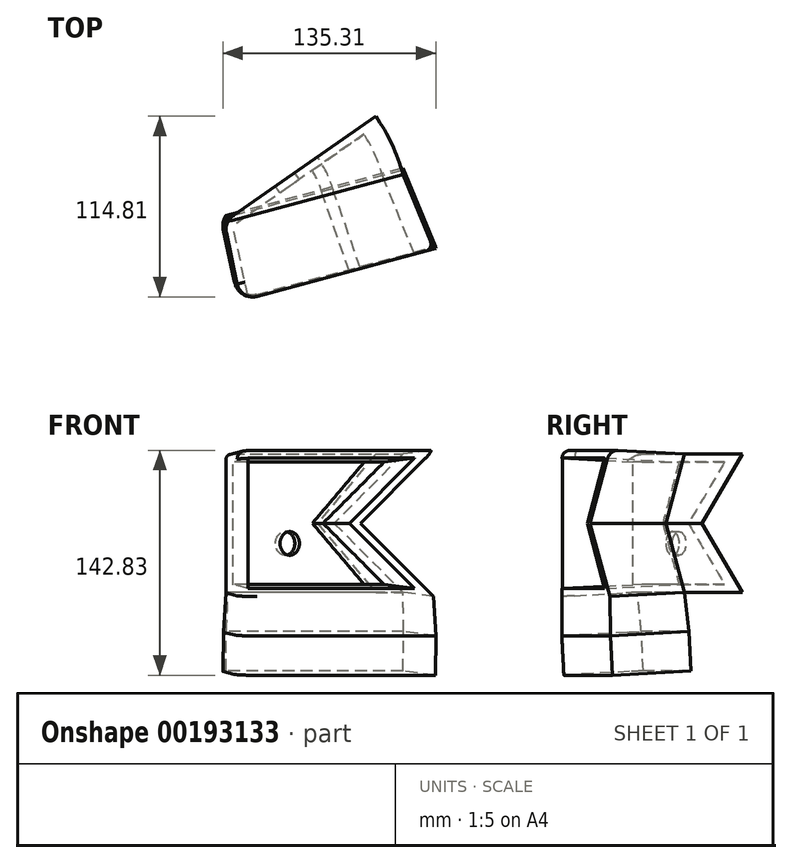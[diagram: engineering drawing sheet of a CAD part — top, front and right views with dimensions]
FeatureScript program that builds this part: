
annotation { "Feature Type Name" : "Feature", "Feature Type Description" : "" }
export const myFeature = defineFeature(function(context is Context, id is Id, definition is map)
    precondition{}
    {
        {
            var Q0;
            Q0=qCreatedBy(makeId("Front.planeOp"),FACE);
            var sketch = newSketch(context, id + "F0", { "sketchPlane" : qUnion([Q0])});
            skLineSegment(sketch, "E0", {"start": v(0, 0) * mm, "end": v(-58.78, 0) * mm});
            skLineSegment(sketch, "E1", {"start": v(-58.78, 0) * mm, "end": v(-58.78, 43.89) * mm});
            skLineSegment(sketch, "E2", {"start": v(-58.78, 43.89) * mm, "end": v(0, 43.89) * mm});
            skLineSegment(sketch, "E3", {"start": v(0, 43.89) * mm, "end": v(-22.61, 21.94) * mm});
            skPoint(sketch, "E3.endSnap0", {"position": v(-58.78, 21.94) * mm});
            skLineSegment(sketch, "E4", {"start": v(-22.61, 21.94) * mm, "end": v(0, 0) * mm});
            skSolve(sketch);
        }
        {
            var Q0;
            Q0=makeQuery(id+"F0.imprint","IMPRINT",FACE,{"disambiguationData":[TD([[makeQuery(id+"F0.imprint","IMPRINT",EDGE,{"derivedFrom":sQuery(id+"F0.wireOp",EDGE,"E0")}),-1.0]])]});
            var Q1;
            Q1=sQuery(id+"F0.wireOp",EDGE,"E1");
            revolve(context, id + "F1", {"entities" : qUnion([Q0]), "axis" : qUnion([Q1]), "revolveType" : RevolveType.TWO_DIRECTIONS, "angle" : 35 * degree, "angleBack" : 15 * degree});
        }
        {
            var Q0;
            Q0=makeQuery(id+"F1.opRevolve","CAP_FACE",FACE,{"disambiguationData":[OSD([sQuery(id+"F0.wireOp",EDGE,"E0"),sQuery(id+"F0.wireOp",EDGE,"E1"),sQuery(id+"F0.wireOp",EDGE,"E2"),sQuery(id+"F0.wireOp",EDGE,"E3"),sQuery(id+"F0.wireOp",EDGE,"E4")])],"isStart":true});
            extrude(context, id + "F2", {"entities" : qUnion([Q0]), "operationType" : NewBodyOperationType.ADD, "depth" : 25.4 * mm, "hasDraft" : true, "draftAngle" : 3 * degree});
        }
        {
            var Q0;
            Q0=makeQuery(id+"F2.opExtrude","CAP_FACE",FACE,{"disambiguationData":[OSD([sQuery(id+"F0.wireOp",EDGE,"E0"),sQuery(id+"F0.wireOp",EDGE,"E1"),sQuery(id+"F0.wireOp",EDGE,"E2"),sQuery(id+"F0.wireOp",EDGE,"E3"),sQuery(id+"F0.wireOp",EDGE,"E4")])],"isStart":false});
            shell(context, id + "F3", {"entities" : qUnion([Q0]), "thickness" : 2.54 * mm});
        }
        {
            var Q0;
            Q0=makeQuery(id+"F2.opExtrude","CAP_EDGE",EDGE,{"disambiguationData":[OSD([sQuery(id+"F0.wireOp",EDGE,"E1")])],"isStart":false});
            fillet(context, id + "F4", {"entities" : qUnion([Q0]), "radius" : 5.08 * mm, "tangentPropagation" : true, "allowEdgeOverflow" : false});
        }
        {
            var Q0;
            {var subQ0=sQuery(id+"F0.wireOp",EDGE,"E1");Q0=makeQuery(id+"F2.boolean.opBoolean","MERGE",EDGE,{"derivedFrom":[makeQuery(id+"F1.opRevolve","CAP_EDGE",EDGE,{"disambiguationData":[OSD([subQ0])],"isStart":true}),makeQuery(id+"F2.opExtrude","CAP_EDGE",EDGE,{"disambiguationData":[OSD([subQ0])],"isStart":true})]});}
            fillet(context, id + "F5", {"entities" : qUnion([Q0]), "radius" : 5.08 * mm, "tangentPropagation" : true, "allowEdgeOverflow" : false});
        }
        {
            var Q0;
            Q0=makeQuery(id+"F2.opExtrude","SWEPT_EDGE",EDGE,{"disambiguationData":[OSD([sQuery(id+"F0.wireOp",EDGE,"E1"),sQuery(id+"F0.wireOp",EDGE,"E2")])]});
            fillet(context, id + "F6", {"entities" : qUnion([Q0]), "radius" : 2.54 * mm, "tangentPropagation" : true, "allowEdgeOverflow" : false});
        }
        {
            var Q0;
            Q0=makeQuery(id+"F1.opRevolve","SWEPT_BODY",BODY,{"disambiguationData":[OSD([sQuery(id+"F0.wireOp",EDGE,"E0"),sQuery(id+"F0.wireOp",EDGE,"E1"),sQuery(id+"F0.wireOp",EDGE,"E2"),sQuery(id+"F0.wireOp",EDGE,"E3"),sQuery(id+"F0.wireOp",EDGE,"E4")])]});
            var Q1;
            {var subQ0=sQuery(id+"F0.wireOp",EDGE,"E2");Q1=makeQuery(id+"F6.opFillet","BLEND_VERTEX",VERTEX,{"blendedFrom":[makeQuery(id+"F2.opExtrude","CAP_EDGE",EDGE,{"disambiguationData":[OSD([subQ0])],"isStart":false}),makeQuery(id+"F2.opExtrude","SWEPT_FACE",FACE,{"disambiguationData":[OSD([sQuery(id+"F0.wireOp",EDGE,"E3")])]}),makeQuery(id+"F2.opExtrude","SWEPT_FACE",FACE,{"disambiguationData":[OSD([subQ0])]})],"blendedInto":[makeQuery(id+"F2.opExtrude","SWEPT_FACE",FACE,{"disambiguationData":[OSD([sQuery(id+"F0.wireOp",EDGE,"E3")])]}),makeQuery(id+"F2.opExtrude","SWEPT_FACE",FACE,{"disambiguationData":[OSD([subQ0])]})]});}
            transform(context, id + "F7", {"entities" : qUnion([Q0]), "transformType" : TransformType.SCALE_UNIFORMLY, "scale" : 2, "scalePoint" : qUnion([Q1]), "makeCopy" : false});
        }
        {
            var Q0;
            Q0=makeQuery(id+"F1.opRevolve","CAP_FACE",FACE,{"disambiguationData":[OSD([sQuery(id+"F0.wireOp",EDGE,"E0"),sQuery(id+"F0.wireOp",EDGE,"E1"),sQuery(id+"F0.wireOp",EDGE,"E2"),sQuery(id+"F0.wireOp",EDGE,"E3"),sQuery(id+"F0.wireOp",EDGE,"E4")])],"isStart":false});
            var sketch = newSketch(context, id + "F8", { "sketchPlane" : qUnion([Q0])});
            skCircle(sketch, "E5", {"center": v(51.07, -14) * mm, "radius": 8.25 * mm});
            skSolve(sketch);
        }
        {
            var Q0;
            Q0=sQuery(id+"F8.wireOp",VERTEX,"E5.center");
            var Q1;
            Q1=makeQuery(id+"F1.opRevolve","SWEPT_BODY",BODY,{"disambiguationData":[OSD([sQuery(id+"F0.wireOp",EDGE,"E0"),sQuery(id+"F0.wireOp",EDGE,"E1"),sQuery(id+"F0.wireOp",EDGE,"E2"),sQuery(id+"F0.wireOp",EDGE,"E3"),sQuery(id+"F0.wireOp",EDGE,"E4")])]});
            hole(context, id + "F9", {"style" : HoleStyle.SIMPLE, "endStyle" : HoleEndStyle.THROUGH, "holeDiameter" : 15 * mm, "isTappedThrough" : true, "tappedDepth" : 12 * mm, "tapClearance" : 3, "locations" : qUnion([Q0]), "scope" : qUnion([Q1])});
        }
        {
            var Q0;
            Q0=makeQuery(id+"F2.opExtrude","SWEPT_FACE",FACE,{"disambiguationData":[OSD([sQuery(id+"F0.wireOp",EDGE,"E0")])]});
            extrude(context, id + "F10", {"entities" : qUnion([Q0]), "operationType" : NewBodyOperationType.ADD, "depth" : 25 * mm, "hasDraft" : true, "draftAngle" : 3 * degree});
        }
        {
            var Q0;
            Q0=makeQuery(id+"F10.opExtrude","CAP_FACE",FACE,{"disambiguationData":[OSD([sQuery(id+"F0.wireOp",EDGE,"E0")])],"isStart":false});
            var sketch = newSketch(context, id + "F11", { "sketchPlane" : qUnion([Q0])});
            skCircle(sketch, "E6", {"center": v(-67.08, 10.93) * mm, "radius": 20.95 * mm});
            skSolve(sketch);
        }
        {
            var Q0;
            Q0=makeQuery(id+"F11.imprint","IMPRINT",FACE,{"disambiguationData":[TD([[makeQuery(id+"F11.imprint","IMPRINT",EDGE,{"derivedFrom":sQuery(id+"F11.wireOp",EDGE,"E6")}),-1.0]])]});
            var Q1;
            Q1=makeQuery(id+"F11.imprint","IMPRINT",FACE,{"disambiguationData":[TD([[makeQuery(id+"F11.imprint","IMPRINT",EDGE,{"derivedFrom":sQuery(id+"F11.wireOp",EDGE,"E6")}),1.0]])]});
            var Q2;
            Q2 = qSketchRegion(id + "F11", true);
            extrude(context, id + "F12", {"entities" : qUnion([Q0, Q1, Q2]), "operationType" : NewBodyOperationType.ADD, "depth" : 25 * mm});
        }
        {
            var Q0;
            Q0=makeQuery(id+"F12.opExtrude","CAP_FACE",FACE,{"disambiguationData":[OSD([sQuery(id+"F0.wireOp",EDGE,"E0"),sQuery(id+"F0.wireOp",EDGE,"E1"),sQuery(id+"F0.wireOp",EDGE,"E4")])],"isStart":false});
            var sketch = newSketch(context, id + "F13", { "sketchPlane" : qUnion([Q0])});
            skCircle(sketch, "E7", {"center": v(-62.28, 7.4) * mm, "radius": 16.87 * mm});
            skSolve(sketch);
        }
        {
            var Q0;
            Q0=sQuery(id+"F13.wireOp",EDGE,"E7");
            extrude(context, id + "F14", {"bodyType" : ToolBodyType.SURFACE, "surfaceEntities" : qUnion([Q0]), "depth" : 25 * mm});
        }
    });
